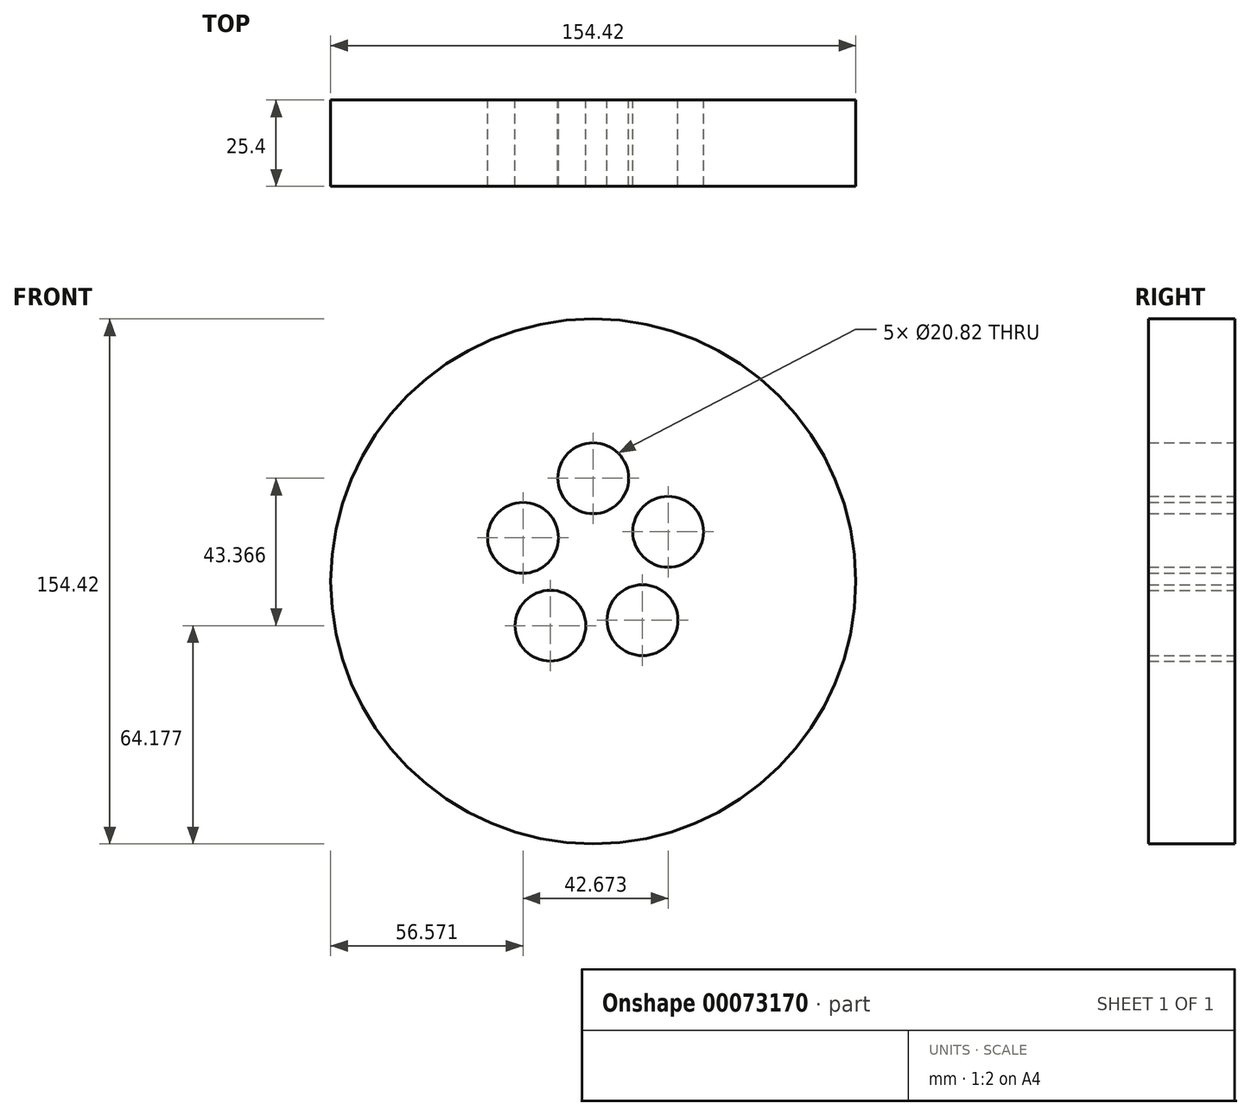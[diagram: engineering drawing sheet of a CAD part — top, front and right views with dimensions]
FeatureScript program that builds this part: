
annotation { "Feature Type Name" : "Feature", "Feature Type Description" : "" }
export const myFeature = defineFeature(function(context is Context, id is Id, definition is map)
    precondition{}
    {
        {
            var Q0;
            Q0=qCreatedBy(makeId("Front.planeOp"),FACE);
            var sketch = newSketch(context, id + "F0", { "sketchPlane" : qUnion([Q0])});
            skCircle(sketch, "E0", {"center": v(0, 0) * mm, "radius": 77.2 * mm});
            skCircle(sketch, "E1", {"center": v(0, 30.33) * mm, "radius": 10.4 * mm});
            skCircle(sketch, "E2", {"center": v(-20.64, 12.82) * mm, "radius": 10.4 * mm});
            skCircle(sketch, "E3", {"center": v(22.03, 14.6) * mm, "radius": 10.4 * mm});
            skCircle(sketch, "E4", {"center": v(-12.6, -13.03) * mm, "radius": 10.4 * mm});
            skCircle(sketch, "E5", {"center": v(14.5, -11.4) * mm, "radius": 10.4 * mm});
            skSolve(sketch);
        }
        {
            var Q0;
            Q0=makeQuery(id+"F0.imprint","IMPRINT",FACE,{"disambiguationData":[TD([[makeQuery(id+"F0.imprint","IMPRINT",EDGE,{"derivedFrom":sQuery(id+"F0.wireOp",EDGE,"E0")}),1.0]])]});
            extrude(context, id + "F1", {"entities" : qUnion([Q0]), "depth" : 25.4 * mm});
        }
    });
